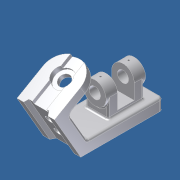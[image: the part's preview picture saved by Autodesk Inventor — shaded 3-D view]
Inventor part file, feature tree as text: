
AUTODESK INVENTOR PART (.ipt)
format: ipt  version: unknown  size: 474,624 bytes
history: native  units: in
note: dims shown in document units (in); Inventor stores cm internally (conversion verified against a paired STEP export)
features: sketch x13, extrude x10, fillet x8, projected_geometry x5, hole x3
ambient origin geometry x8: Origin, YZ Plane, XZ Plane, XY Plane, X Axis, Y Axis, Z Axis, Center Point
bodies: Solid1 (feature_tree)
feature tree (39):
  extrude  "Extrusion1"  Depth=0.75in
  hole  "Hole1"  [1 undecoded]
  extrude  "Extrusion3"  Depth=2.5in TaperAngle=0.0deg
  extrude  "Extrusion4"  Depth=0.4375in
  hole  "Hole2"  [1 undecoded]
  extrude  "Extrusion5"  Depth=0.25in
  extrude  "Extrusion6"  Depth=1.125in
  extrude  "Extrusion7"  Depth=1.125in
  extrude  "Extrusion8"  Depth=0.6875in
  extrude  "Extrusion9"  Depth=0.5in
  extrude  "Extrusion10"  Depth=0.25in TaperAngle=0.0deg
  extrude  "Extrusion11"  Depth=0.125in
  fillet  "Fillet1"  Radius=0.25in
  fillet  "Fillet2"  Radius=0.625in
  fillet  "Fillet4"  Radius=0.625in
  fillet  "Fillet5"  Radius=1.75in
  fillet  "Fillet6"  Radius=2.0in
  fillet  "Fillet7"  Radius=1.25in
  fillet  "Fillet8"  Radius=0.75in
  fillet  "Fillet9"  Radius=2.625in
  hole  "Hole3"  [1 undecoded]
  sketch  "Sketch1"  dims[d0=5.5in d1=0.75in]
  sketch  "Sketch3"  dims[d2=3.5in d3=60.0deg]
  sketch  "Sketch4"  dims[d6=0.6875in d7=2.5in d8=0.0in]
  sketch  "Sketch5"  dims[d13=0.75in d14=0.75in d15=1.25in d16=0.375in d17=0.5635in d18=0.6875in d19=0.8108in d21=0.4375in]
  projected_geometry  "Projected Loop1"
  projected_geometry  "Projected Loop2"
  sketch  "Sketch6"  dims[d22=0.25in d23=0.0in d25=0.4375in]
  sketch  "Sketch7"  dims[d26=0.4375in d29=0.25in]
  sketch  "Sketch8"  dims[d30=3.5in d31=0.0in d32=1.125in]
  sketch  "Sketch9"  dims[d33=1.25in d34=1.125in]
  sketch  "Sketch10"  dims[d35=1.25in]
  projected_geometry  "Projected Loop3"
  sketch  "Sketch11"  dims[d36=0.5in d37=0.75in d38=1.25in d39=0.375in d40=0.5635in d41=0.6875in d42=0.8108in d43=0.6875in]
  sketch  "Sketch12"  dims[d44=0.5in d45=0.5in]
  sketch  "Sketch13"  dims[d46=2.625in d47=0.25in d48=0.0in]
  projected_geometry  "Projected Loop4"
  projected_geometry  "Projected Loop5"
  sketch  "Sketch14"  dims[d49=0.125in d50=0.125in d51=0.25in d52=0.0in d53=0.625in d54=0.625in d55=1.75in d56=0.0in d57=2.0in d58=1.25in d60=0.75in d61=2.625in d62=0.0in d63=1.5in d64=2.375in d65=0.0in d66=0.125in d67=0.0in d68=0.125in d69=0.0in d70=0.25in d71=0.25in d73=0.125in d74=3.25in d75=1.25in d76=0.125in d77=0.125in d78=0.125in d79=0.125in d80=0.375in d81=0.375in d82=0.75in d83=0.75in d84=0.125in d85=0.75in d86=0.375in d87=0.25in d88=0.5635in d89=0.6in d90=0.8108in]
note: 3 required parameter values undecoded (feature->parameter linkage not recoverable at this tier; creation-order binding heuristic only, values carry confidence <= 0.55)
